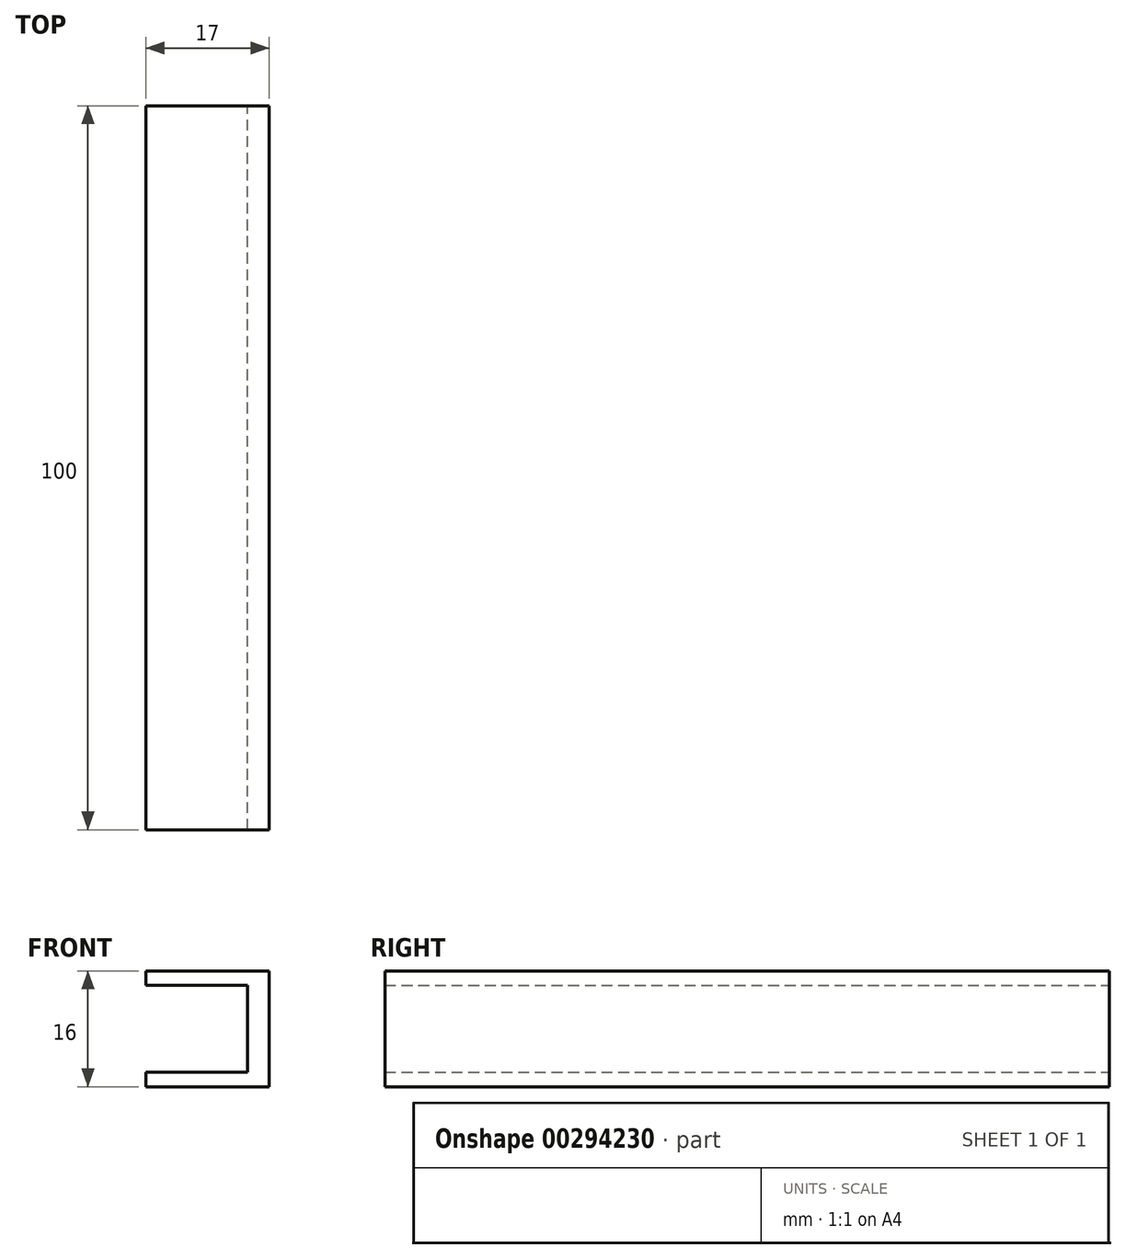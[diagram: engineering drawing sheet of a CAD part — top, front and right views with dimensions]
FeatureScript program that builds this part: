
annotation { "Feature Type Name" : "Feature", "Feature Type Description" : "" }
export const myFeature = defineFeature(function(context is Context, id is Id, definition is map)
    precondition{}
    {
        {
            var Q0;
            Q0=qCreatedBy(makeId("Front.planeOp"),FACE);
            var sketch = newSketch(context, id + "F0", { "sketchPlane" : qUnion([Q0])});
            skLineSegment(sketch, "E0.bottom", {"start": v(0, 0) * mm, "end": v(17, 0) * mm});
            skLineSegment(sketch, "E0.top", {"start": v(0, 16) * mm, "end": v(17, 16) * mm});
            skLineSegment(sketch, "E0.left", {"start": v(0, 0) * mm, "end": v(0, 2) * mm});
            skLineSegment(sketch, "E0.right", {"start": v(17, 0) * mm, "end": v(17, 16) * mm});
            skLineSegment(sketch, "E1", {"start": v(0, 14) * mm, "end": v(14, 14) * mm});
            skLineSegment(sketch, "E2", {"start": v(14, 14) * mm, "end": v(14, 2) * mm});
            skLineSegment(sketch, "E3", {"start": v(14, 2) * mm, "end": v(0, 2) * mm});
            skLineSegment(sketch, "E4.trimOffspring", {"start": v(0, 14) * mm, "end": v(0, 16) * mm});
            skSolve(sketch);
        }
        {
            var Q0;
            Q0 = qSketchRegion(id + "F0", true);
            extrude(context, id + "F1", {"entities" : qUnion([Q0]), "depth" : 100 * mm});
        }
    });
